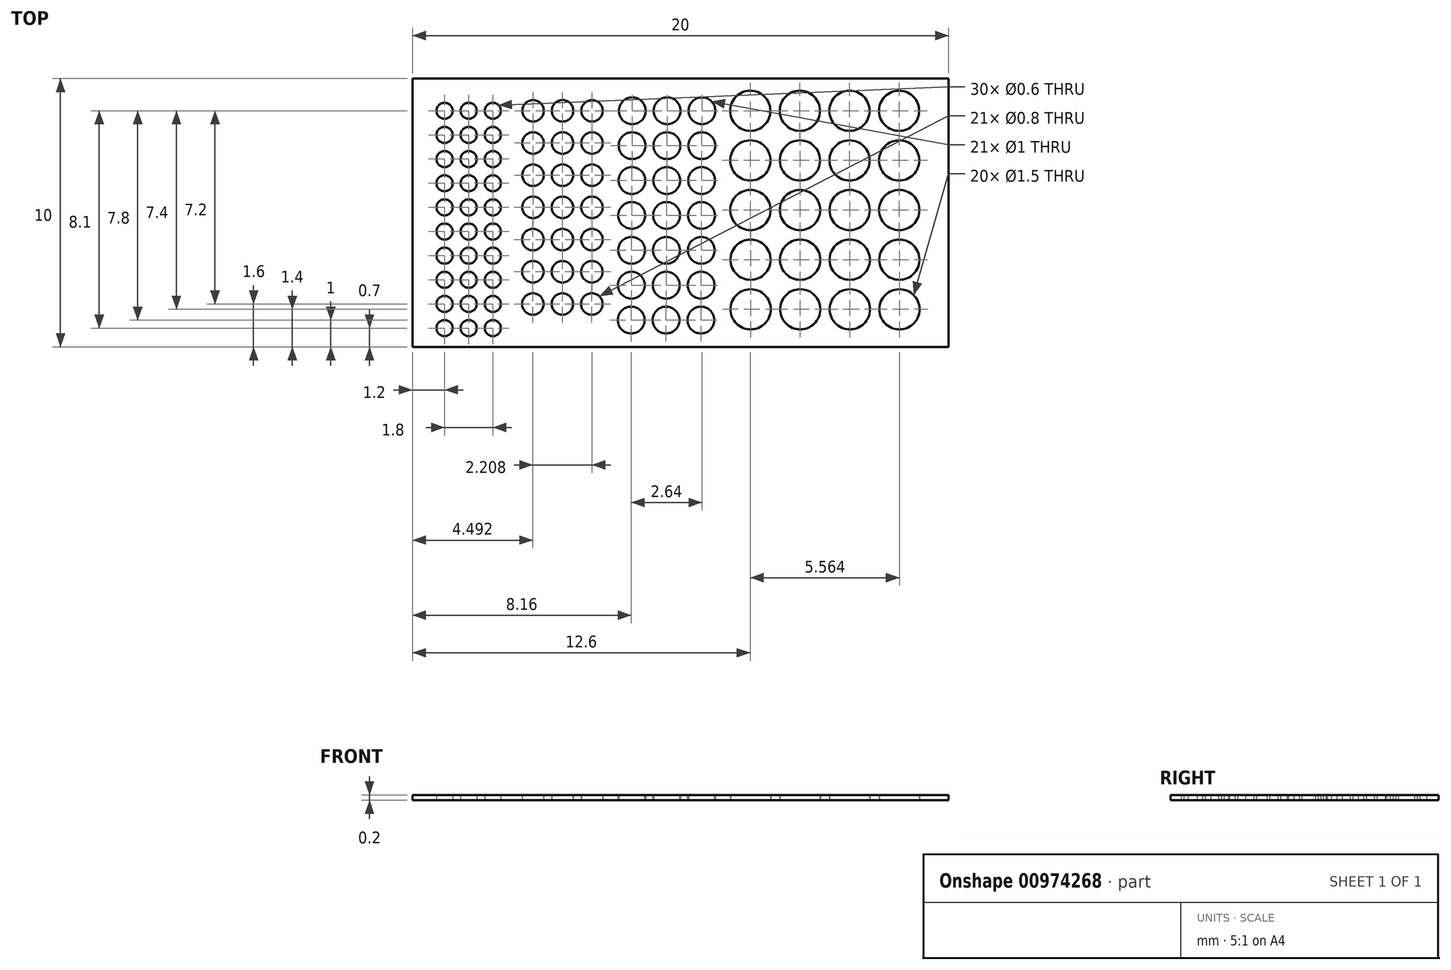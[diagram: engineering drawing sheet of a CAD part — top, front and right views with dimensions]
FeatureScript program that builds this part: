
annotation { "Feature Type Name" : "Feature", "Feature Type Description" : "" }
export const myFeature = defineFeature(function(context is Context, id is Id, definition is map)
    precondition{}
    {
        {
            var Q0;
            Q0=qCreatedBy(makeId("Top.planeOp"),FACE);
            var sketch = newSketch(context, id + "F0", { "sketchPlane" : qUnion([Q0])});
            skLineSegment(sketch, "E0.bottom", {"start": v(0, 0) * mm, "end": v(20, 0) * mm});
            skLineSegment(sketch, "E0.top", {"start": v(0, -10) * mm, "end": v(20, -10) * mm});
            skLineSegment(sketch, "E0.left", {"start": v(0, 0) * mm, "end": v(0, -10) * mm});
            skLineSegment(sketch, "E0.right", {"start": v(20, 0) * mm, "end": v(20, -10) * mm});
            skEllipse(sketch, "E1", {"center": v(1.2, -1.2) * mm, "majorRadius": 0.3 * mm, "minorRadius": 0.3 * mm, "majorAxis": v(0.93, 0.38)});
            skEllipse(sketch, "E2.1.0.0", {"center": v(2.1, -1.2) * mm, "majorRadius": 0.3 * mm, "minorRadius": 0.3 * mm, "majorAxis": v(0.93, 0.38)});
            skEllipse(sketch, "E2.2.0.0", {"center": v(3, -1.2) * mm, "majorRadius": 0.3 * mm, "minorRadius": 0.3 * mm, "majorAxis": v(0.93, 0.38)});
            skLineSegment(sketch, "E2.direction1", {"start": v(1.2, -1.2) * mm, "end": v(2.1, -1.2) * mm, "construction": true});
            skCircle(sketch, "E3", {"center": v(4.5, -1.2) * mm, "radius": 0.4 * mm});
            skCircle(sketch, "E4", {"center": v(8.2, -1.2) * mm, "radius": 0.5 * mm});
            skCircle(sketch, "E5", {"center": v(12.6, -1.2) * mm, "radius": 0.75 * mm});
            skCircle(sketch, "E6.1.0.0", {"center": v(5.6, -1.2) * mm, "radius": 0.4 * mm});
            skCircle(sketch, "E6.2.0.0", {"center": v(6.7, -1.2) * mm, "radius": 0.4 * mm});
            skLineSegment(sketch, "E6.direction1", {"start": v(4.5, -1.2) * mm, "end": v(5.6, -1.2) * mm, "construction": true});
            skCircle(sketch, "E7.1.0.0", {"center": v(4.5, -2.4) * mm, "radius": 0.4 * mm});
            skLineSegment(sketch, "E7.1.0.1", {"start": v(4.5, -2.4) * mm, "end": v(5.6, -2.4) * mm, "construction": true});
            skCircle(sketch, "E7.1.0.2", {"center": v(5.6, -2.4) * mm, "radius": 0.4 * mm});
            skCircle(sketch, "E7.1.0.3", {"center": v(6.7, -2.4) * mm, "radius": 0.4 * mm});
            skCircle(sketch, "E7.2.0.0", {"center": v(4.5, -3.6) * mm, "radius": 0.4 * mm});
            skLineSegment(sketch, "E7.2.0.1", {"start": v(4.5, -3.6) * mm, "end": v(5.6, -3.6) * mm, "construction": true});
            skCircle(sketch, "E7.2.0.2", {"center": v(5.6, -3.6) * mm, "radius": 0.4 * mm});
            skCircle(sketch, "E7.2.0.3", {"center": v(6.7, -3.6) * mm, "radius": 0.4 * mm});
            skCircle(sketch, "E7.3.0.0", {"center": v(4.5, -4.8) * mm, "radius": 0.4 * mm});
            skLineSegment(sketch, "E7.3.0.1", {"start": v(4.5, -4.8) * mm, "end": v(5.6, -4.8) * mm, "construction": true});
            skCircle(sketch, "E7.3.0.2", {"center": v(5.6, -4.8) * mm, "radius": 0.4 * mm});
            skCircle(sketch, "E7.3.0.3", {"center": v(6.7, -4.8) * mm, "radius": 0.4 * mm});
            skCircle(sketch, "E7.4.0.0", {"center": v(4.5, -6) * mm, "radius": 0.4 * mm});
            skLineSegment(sketch, "E7.4.0.1", {"start": v(4.5, -6) * mm, "end": v(5.6, -6) * mm, "construction": true});
            skCircle(sketch, "E7.4.0.2", {"center": v(5.6, -6) * mm, "radius": 0.4 * mm});
            skCircle(sketch, "E7.4.0.3", {"center": v(6.7, -6) * mm, "radius": 0.4 * mm});
            skCircle(sketch, "E7.5.0.0", {"center": v(4.5, -7.2) * mm, "radius": 0.4 * mm});
            skLineSegment(sketch, "E7.5.0.1", {"start": v(4.5, -7.2) * mm, "end": v(5.6, -7.2) * mm, "construction": true});
            skCircle(sketch, "E7.5.0.2", {"center": v(5.6, -7.2) * mm, "radius": 0.4 * mm});
            skCircle(sketch, "E7.5.0.3", {"center": v(6.7, -7.2) * mm, "radius": 0.4 * mm});
            skCircle(sketch, "E7.6.0.0", {"center": v(4.5, -8.4) * mm, "radius": 0.4 * mm});
            skLineSegment(sketch, "E7.6.0.1", {"start": v(4.5, -8.4) * mm, "end": v(5.6, -8.4) * mm, "construction": true});
            skCircle(sketch, "E7.6.0.2", {"center": v(5.6, -8.4) * mm, "radius": 0.4 * mm});
            skCircle(sketch, "E7.6.0.3", {"center": v(6.7, -8.4) * mm, "radius": 0.4 * mm});
            skLineSegment(sketch, "E7.direction1", {"start": v(4.5, -1.2) * mm, "end": v(4.5, -2.4) * mm, "construction": true});
            skCircle(sketch, "E8.1.0.0", {"center": v(14.45, -1.2) * mm, "radius": 0.75 * mm});
            skCircle(sketch, "E8.2.0.0", {"center": v(16.3, -1.2) * mm, "radius": 0.75 * mm});
            skCircle(sketch, "E8.3.0.0", {"center": v(18.15, -1.2) * mm, "radius": 0.75 * mm});
            skLineSegment(sketch, "E8.direction1", {"start": v(12.6, -1.2) * mm, "end": v(14.45, -1.2) * mm, "construction": true});
            skCircle(sketch, "E9.1.0.0", {"center": v(18.15, -3.05) * mm, "radius": 0.75 * mm});
            skLineSegment(sketch, "E9.1.0.1", {"start": v(12.6, -3.05) * mm, "end": v(14.45, -3.05) * mm, "construction": true});
            skCircle(sketch, "E9.1.0.2", {"center": v(14.45, -3.05) * mm, "radius": 0.75 * mm});
            skCircle(sketch, "E9.1.0.3", {"center": v(12.6, -3.05) * mm, "radius": 0.75 * mm});
            skCircle(sketch, "E9.1.0.4", {"center": v(16.3, -3.05) * mm, "radius": 0.75 * mm});
            skCircle(sketch, "E9.2.0.0", {"center": v(18.16, -4.9) * mm, "radius": 0.75 * mm});
            skLineSegment(sketch, "E9.2.0.1", {"start": v(12.6, -4.9) * mm, "end": v(14.46, -4.9) * mm, "construction": true});
            skCircle(sketch, "E9.2.0.2", {"center": v(14.46, -4.9) * mm, "radius": 0.75 * mm});
            skCircle(sketch, "E9.2.0.3", {"center": v(12.6, -4.9) * mm, "radius": 0.75 * mm});
            skCircle(sketch, "E9.2.0.4", {"center": v(16.3, -4.9) * mm, "radius": 0.75 * mm});
            skCircle(sketch, "E9.3.0.0", {"center": v(18.16, -6.75) * mm, "radius": 0.75 * mm});
            skLineSegment(sketch, "E9.3.0.1", {"start": v(12.61, -6.75) * mm, "end": v(14.46, -6.75) * mm, "construction": true});
            skCircle(sketch, "E9.3.0.2", {"center": v(14.46, -6.75) * mm, "radius": 0.75 * mm});
            skCircle(sketch, "E9.3.0.3", {"center": v(12.61, -6.75) * mm, "radius": 0.75 * mm});
            skCircle(sketch, "E9.3.0.4", {"center": v(16.31, -6.75) * mm, "radius": 0.75 * mm});
            skCircle(sketch, "E9.4.0.0", {"center": v(18.16, -8.6) * mm, "radius": 0.75 * mm});
            skLineSegment(sketch, "E9.4.0.1", {"start": v(12.61, -8.6) * mm, "end": v(14.46, -8.6) * mm, "construction": true});
            skCircle(sketch, "E9.4.0.2", {"center": v(14.46, -8.6) * mm, "radius": 0.75 * mm});
            skCircle(sketch, "E9.4.0.3", {"center": v(12.61, -8.6) * mm, "radius": 0.75 * mm});
            skCircle(sketch, "E9.4.0.4", {"center": v(16.31, -8.6) * mm, "radius": 0.75 * mm});
            skLineSegment(sketch, "E9.direction1", {"start": v(12.6, -1.2) * mm, "end": v(12.6, -3.05) * mm, "construction": true});
            skCircle(sketch, "E10.1.0.0", {"center": v(9.5, -1.2) * mm, "radius": 0.5 * mm});
            skCircle(sketch, "E10.2.0.0", {"center": v(10.8, -1.2) * mm, "radius": 0.5 * mm});
            skLineSegment(sketch, "E10.direction1", {"start": v(8.2, -1.2) * mm, "end": v(9.5, -1.2) * mm, "construction": true});
            skCircle(sketch, "E11.1.0.0", {"center": v(9.5, -2.5) * mm, "radius": 0.5 * mm});
            skCircle(sketch, "E11.1.0.1", {"center": v(10.8, -2.5) * mm, "radius": 0.5 * mm});
            skCircle(sketch, "E11.1.0.2", {"center": v(8.2, -2.5) * mm, "radius": 0.5 * mm});
            skLineSegment(sketch, "E11.1.0.3", {"start": v(8.2, -2.5) * mm, "end": v(9.5, -2.5) * mm, "construction": true});
            skCircle(sketch, "E11.2.0.0", {"center": v(9.49, -3.8) * mm, "radius": 0.5 * mm});
            skCircle(sketch, "E11.2.0.1", {"center": v(10.79, -3.8) * mm, "radius": 0.5 * mm});
            skCircle(sketch, "E11.2.0.2", {"center": v(8.19, -3.8) * mm, "radius": 0.5 * mm});
            skLineSegment(sketch, "E11.2.0.3", {"start": v(8.19, -3.8) * mm, "end": v(9.49, -3.8) * mm, "construction": true});
            skCircle(sketch, "E11.3.0.0", {"center": v(9.48, -5.1) * mm, "radius": 0.5 * mm});
            skCircle(sketch, "E11.3.0.1", {"center": v(10.78, -5.1) * mm, "radius": 0.5 * mm});
            skCircle(sketch, "E11.3.0.2", {"center": v(8.18, -5.1) * mm, "radius": 0.5 * mm});
            skLineSegment(sketch, "E11.3.0.3", {"start": v(8.18, -5.1) * mm, "end": v(9.48, -5.1) * mm, "construction": true});
            skCircle(sketch, "E11.4.0.0", {"center": v(9.47, -6.4) * mm, "radius": 0.5 * mm});
            skCircle(sketch, "E11.4.0.1", {"center": v(10.77, -6.4) * mm, "radius": 0.5 * mm});
            skCircle(sketch, "E11.4.0.2", {"center": v(8.17, -6.4) * mm, "radius": 0.5 * mm});
            skLineSegment(sketch, "E11.4.0.3", {"start": v(8.17, -6.4) * mm, "end": v(9.47, -6.4) * mm, "construction": true});
            skCircle(sketch, "E11.5.0.0", {"center": v(9.47, -7.7) * mm, "radius": 0.5 * mm});
            skCircle(sketch, "E11.5.0.1", {"center": v(10.77, -7.7) * mm, "radius": 0.5 * mm});
            skCircle(sketch, "E11.5.0.2", {"center": v(8.17, -7.7) * mm, "radius": 0.5 * mm});
            skLineSegment(sketch, "E11.5.0.3", {"start": v(8.17, -7.7) * mm, "end": v(9.47, -7.7) * mm, "construction": true});
            skCircle(sketch, "E11.6.0.0", {"center": v(9.46, -9) * mm, "radius": 0.5 * mm});
            skCircle(sketch, "E11.6.0.1", {"center": v(10.76, -9) * mm, "radius": 0.5 * mm});
            skCircle(sketch, "E11.6.0.2", {"center": v(8.16, -9) * mm, "radius": 0.5 * mm});
            skLineSegment(sketch, "E11.6.0.3", {"start": v(8.16, -9) * mm, "end": v(9.46, -9) * mm, "construction": true});
            skLineSegment(sketch, "E11.direction1", {"start": v(8.2, -1.2) * mm, "end": v(8.2, -2.5) * mm, "construction": true});
            skEllipse(sketch, "E12.MirrorC", {"center": v(2.1, -1.2) * mm, "majorRadius": 0.3 * mm, "minorRadius": 0.3 * mm, "majorAxis": v(0.93, -0.38)});
            skEllipse(sketch, "E13.MirrorC", {"center": v(1.2, -1.2) * mm, "majorRadius": 0.3 * mm, "minorRadius": 0.3 * mm, "majorAxis": v(0.93, -0.38)});
            skEllipse(sketch, "E14.MirrorC", {"center": v(3, -1.2) * mm, "majorRadius": 0.3 * mm, "minorRadius": 0.3 * mm, "majorAxis": v(0.93, -0.38)});
            skEllipse(sketch, "E15.1.0.0", {"center": v(2.1, -2.1) * mm, "majorRadius": 0.3 * mm, "minorRadius": 0.3 * mm, "majorAxis": v(0.93, 0.38)});
            skEllipse(sketch, "E15.1.0.1", {"center": v(1.2, -2.1) * mm, "majorRadius": 0.3 * mm, "minorRadius": 0.3 * mm, "majorAxis": v(0.93, -0.38)});
            skEllipse(sketch, "E15.1.0.2", {"center": v(3, -2.1) * mm, "majorRadius": 0.3 * mm, "minorRadius": 0.3 * mm, "majorAxis": v(0.93, 0.38)});
            skLineSegment(sketch, "E15.1.0.3", {"start": v(1.2, -2.1) * mm, "end": v(2.1, -2.1) * mm, "construction": true});
            skEllipse(sketch, "E15.1.0.4", {"center": v(1.2, -2.1) * mm, "majorRadius": 0.3 * mm, "minorRadius": 0.3 * mm, "majorAxis": v(0.93, 0.38)});
            skEllipse(sketch, "E15.1.0.5", {"center": v(3, -2.1) * mm, "majorRadius": 0.3 * mm, "minorRadius": 0.3 * mm, "majorAxis": v(0.93, -0.38)});
            skEllipse(sketch, "E15.1.0.6", {"center": v(2.1, -2.1) * mm, "majorRadius": 0.3 * mm, "minorRadius": 0.3 * mm, "majorAxis": v(0.93, -0.38)});
            skEllipse(sketch, "E15.2.0.0", {"center": v(2.1, -3) * mm, "majorRadius": 0.3 * mm, "minorRadius": 0.3 * mm, "majorAxis": v(0.93, 0.38)});
            skEllipse(sketch, "E15.2.0.1", {"center": v(1.2, -3) * mm, "majorRadius": 0.3 * mm, "minorRadius": 0.3 * mm, "majorAxis": v(0.93, -0.38)});
            skEllipse(sketch, "E15.2.0.2", {"center": v(3, -3) * mm, "majorRadius": 0.3 * mm, "minorRadius": 0.3 * mm, "majorAxis": v(0.93, 0.38)});
            skLineSegment(sketch, "E15.2.0.3", {"start": v(1.2, -3) * mm, "end": v(2.1, -3) * mm, "construction": true});
            skEllipse(sketch, "E15.2.0.4", {"center": v(1.2, -3) * mm, "majorRadius": 0.3 * mm, "minorRadius": 0.3 * mm, "majorAxis": v(0.93, 0.38)});
            skEllipse(sketch, "E15.2.0.5", {"center": v(3, -3) * mm, "majorRadius": 0.3 * mm, "minorRadius": 0.3 * mm, "majorAxis": v(0.93, -0.38)});
            skEllipse(sketch, "E15.2.0.6", {"center": v(2.1, -3) * mm, "majorRadius": 0.3 * mm, "minorRadius": 0.3 * mm, "majorAxis": v(0.93, -0.38)});
            skEllipse(sketch, "E15.3.0.0", {"center": v(2.1, -3.9) * mm, "majorRadius": 0.3 * mm, "minorRadius": 0.3 * mm, "majorAxis": v(0.93, 0.38)});
            skEllipse(sketch, "E15.3.0.1", {"center": v(1.2, -3.9) * mm, "majorRadius": 0.3 * mm, "minorRadius": 0.3 * mm, "majorAxis": v(0.93, -0.38)});
            skEllipse(sketch, "E15.3.0.2", {"center": v(3, -3.9) * mm, "majorRadius": 0.3 * mm, "minorRadius": 0.3 * mm, "majorAxis": v(0.93, 0.38)});
            skLineSegment(sketch, "E15.3.0.3", {"start": v(1.2, -3.9) * mm, "end": v(2.1, -3.9) * mm, "construction": true});
            skEllipse(sketch, "E15.3.0.4", {"center": v(1.2, -3.9) * mm, "majorRadius": 0.3 * mm, "minorRadius": 0.3 * mm, "majorAxis": v(0.93, 0.38)});
            skEllipse(sketch, "E15.3.0.5", {"center": v(3, -3.9) * mm, "majorRadius": 0.3 * mm, "minorRadius": 0.3 * mm, "majorAxis": v(0.93, -0.38)});
            skEllipse(sketch, "E15.3.0.6", {"center": v(2.1, -3.9) * mm, "majorRadius": 0.3 * mm, "minorRadius": 0.3 * mm, "majorAxis": v(0.93, -0.38)});
            skEllipse(sketch, "E15.4.0.0", {"center": v(2.1, -4.8) * mm, "majorRadius": 0.3 * mm, "minorRadius": 0.3 * mm, "majorAxis": v(0.93, 0.38)});
            skEllipse(sketch, "E15.4.0.1", {"center": v(1.2, -4.8) * mm, "majorRadius": 0.3 * mm, "minorRadius": 0.3 * mm, "majorAxis": v(0.93, -0.38)});
            skEllipse(sketch, "E15.4.0.2", {"center": v(3, -4.8) * mm, "majorRadius": 0.3 * mm, "minorRadius": 0.3 * mm, "majorAxis": v(0.93, 0.38)});
            skLineSegment(sketch, "E15.4.0.3", {"start": v(1.2, -4.8) * mm, "end": v(2.1, -4.8) * mm, "construction": true});
            skEllipse(sketch, "E15.4.0.4", {"center": v(1.2, -4.8) * mm, "majorRadius": 0.3 * mm, "minorRadius": 0.3 * mm, "majorAxis": v(0.93, 0.38)});
            skEllipse(sketch, "E15.4.0.5", {"center": v(3, -4.8) * mm, "majorRadius": 0.3 * mm, "minorRadius": 0.3 * mm, "majorAxis": v(0.93, -0.38)});
            skEllipse(sketch, "E15.4.0.6", {"center": v(2.1, -4.8) * mm, "majorRadius": 0.3 * mm, "minorRadius": 0.3 * mm, "majorAxis": v(0.93, -0.38)});
            skEllipse(sketch, "E15.5.0.0", {"center": v(2.1, -5.7) * mm, "majorRadius": 0.3 * mm, "minorRadius": 0.3 * mm, "majorAxis": v(0.93, 0.38)});
            skEllipse(sketch, "E15.5.0.1", {"center": v(1.2, -5.7) * mm, "majorRadius": 0.3 * mm, "minorRadius": 0.3 * mm, "majorAxis": v(0.93, -0.38)});
            skEllipse(sketch, "E15.5.0.2", {"center": v(3, -5.7) * mm, "majorRadius": 0.3 * mm, "minorRadius": 0.3 * mm, "majorAxis": v(0.93, 0.38)});
            skLineSegment(sketch, "E15.5.0.3", {"start": v(1.2, -5.7) * mm, "end": v(2.1, -5.7) * mm, "construction": true});
            skEllipse(sketch, "E15.5.0.4", {"center": v(1.2, -5.7) * mm, "majorRadius": 0.3 * mm, "minorRadius": 0.3 * mm, "majorAxis": v(0.93, 0.38)});
            skEllipse(sketch, "E15.5.0.5", {"center": v(3, -5.7) * mm, "majorRadius": 0.3 * mm, "minorRadius": 0.3 * mm, "majorAxis": v(0.93, -0.38)});
            skEllipse(sketch, "E15.5.0.6", {"center": v(2.1, -5.7) * mm, "majorRadius": 0.3 * mm, "minorRadius": 0.3 * mm, "majorAxis": v(0.93, -0.38)});
            skEllipse(sketch, "E15.6.0.0", {"center": v(2.1, -6.6) * mm, "majorRadius": 0.3 * mm, "minorRadius": 0.3 * mm, "majorAxis": v(0.93, 0.38)});
            skEllipse(sketch, "E15.6.0.1", {"center": v(1.2, -6.6) * mm, "majorRadius": 0.3 * mm, "minorRadius": 0.3 * mm, "majorAxis": v(0.93, -0.38)});
            skEllipse(sketch, "E15.6.0.2", {"center": v(3, -6.6) * mm, "majorRadius": 0.3 * mm, "minorRadius": 0.3 * mm, "majorAxis": v(0.93, 0.38)});
            skLineSegment(sketch, "E15.6.0.3", {"start": v(1.2, -6.6) * mm, "end": v(2.1, -6.6) * mm, "construction": true});
            skEllipse(sketch, "E15.6.0.4", {"center": v(1.2, -6.6) * mm, "majorRadius": 0.3 * mm, "minorRadius": 0.3 * mm, "majorAxis": v(0.93, 0.38)});
            skEllipse(sketch, "E15.6.0.5", {"center": v(3, -6.6) * mm, "majorRadius": 0.3 * mm, "minorRadius": 0.3 * mm, "majorAxis": v(0.93, -0.38)});
            skEllipse(sketch, "E15.6.0.6", {"center": v(2.1, -6.6) * mm, "majorRadius": 0.3 * mm, "minorRadius": 0.3 * mm, "majorAxis": v(0.93, -0.38)});
            skEllipse(sketch, "E15.7.0.0", {"center": v(2.1, -7.5) * mm, "majorRadius": 0.3 * mm, "minorRadius": 0.3 * mm, "majorAxis": v(0.93, 0.38)});
            skEllipse(sketch, "E15.7.0.1", {"center": v(1.2, -7.5) * mm, "majorRadius": 0.3 * mm, "minorRadius": 0.3 * mm, "majorAxis": v(0.93, -0.38)});
            skEllipse(sketch, "E15.7.0.2", {"center": v(3, -7.5) * mm, "majorRadius": 0.3 * mm, "minorRadius": 0.3 * mm, "majorAxis": v(0.93, 0.38)});
            skLineSegment(sketch, "E15.7.0.3", {"start": v(1.2, -7.5) * mm, "end": v(2.1, -7.5) * mm, "construction": true});
            skEllipse(sketch, "E15.7.0.4", {"center": v(1.2, -7.5) * mm, "majorRadius": 0.3 * mm, "minorRadius": 0.3 * mm, "majorAxis": v(0.93, 0.38)});
            skEllipse(sketch, "E15.7.0.5", {"center": v(3, -7.5) * mm, "majorRadius": 0.3 * mm, "minorRadius": 0.3 * mm, "majorAxis": v(0.93, -0.38)});
            skEllipse(sketch, "E15.7.0.6", {"center": v(2.1, -7.5) * mm, "majorRadius": 0.3 * mm, "minorRadius": 0.3 * mm, "majorAxis": v(0.93, -0.38)});
            skEllipse(sketch, "E15.8.0.0", {"center": v(2.1, -8.4) * mm, "majorRadius": 0.3 * mm, "minorRadius": 0.3 * mm, "majorAxis": v(0.93, 0.38)});
            skEllipse(sketch, "E15.8.0.1", {"center": v(1.2, -8.4) * mm, "majorRadius": 0.3 * mm, "minorRadius": 0.3 * mm, "majorAxis": v(0.93, -0.38)});
            skEllipse(sketch, "E15.8.0.2", {"center": v(3, -8.4) * mm, "majorRadius": 0.3 * mm, "minorRadius": 0.3 * mm, "majorAxis": v(0.93, 0.38)});
            skLineSegment(sketch, "E15.8.0.3", {"start": v(1.2, -8.4) * mm, "end": v(2.1, -8.4) * mm, "construction": true});
            skEllipse(sketch, "E15.8.0.4", {"center": v(1.2, -8.4) * mm, "majorRadius": 0.3 * mm, "minorRadius": 0.3 * mm, "majorAxis": v(0.93, 0.38)});
            skEllipse(sketch, "E15.8.0.5", {"center": v(3, -8.4) * mm, "majorRadius": 0.3 * mm, "minorRadius": 0.3 * mm, "majorAxis": v(0.93, -0.38)});
            skEllipse(sketch, "E15.8.0.6", {"center": v(2.1, -8.4) * mm, "majorRadius": 0.3 * mm, "minorRadius": 0.3 * mm, "majorAxis": v(0.93, -0.38)});
            skLineSegment(sketch, "E15.direction1", {"start": v(1.2, -1.2) * mm, "end": v(1.2, -2.1) * mm, "construction": true});
            skEllipse(sketch, "E16.0.9.0", {"center": v(2.1, -9.3) * mm, "majorRadius": 0.3 * mm, "minorRadius": 0.3 * mm, "majorAxis": v(0.93, 0.38)});
            skEllipse(sketch, "E16.2.9.0", {"center": v(1.2, -9.3) * mm, "majorRadius": 0.3 * mm, "minorRadius": 0.3 * mm, "majorAxis": v(0.93, -0.38)});
            skEllipse(sketch, "E16.4.9.0", {"center": v(3, -9.3) * mm, "majorRadius": 0.3 * mm, "minorRadius": 0.3 * mm, "majorAxis": v(0.93, 0.38)});
            skLineSegment(sketch, "E16.6.9.0", {"start": v(1.2, -9.3) * mm, "end": v(2.1, -9.3) * mm, "construction": true});
            skEllipse(sketch, "E16.9.9.0", {"center": v(1.2, -9.3) * mm, "majorRadius": 0.3 * mm, "minorRadius": 0.3 * mm, "majorAxis": v(0.93, 0.38)});
            skEllipse(sketch, "E16.11.9.0", {"center": v(3, -9.3) * mm, "majorRadius": 0.3 * mm, "minorRadius": 0.3 * mm, "majorAxis": v(0.93, -0.38)});
            skEllipse(sketch, "E16.13.9.0", {"center": v(2.1, -9.3) * mm, "majorRadius": 0.3 * mm, "minorRadius": 0.3 * mm, "majorAxis": v(0.93, -0.38)});
            skSolve(sketch);
        }
        {
            var Q0;
            Q0=makeQuery(id+"F0.imprint","IMPRINT",FACE,{"disambiguationData":[TD([[makeQuery(id+"F0.imprint","IMPRINT",EDGE,{"derivedFrom":sQuery(id+"F0.wireOp",EDGE,"E0.bottom")}),-1.0]])]});
            extrude(context, id + "F1", {"entities" : qUnion([Q0]), "depth" : 0.2 * mm, "offsetDistance" : 25.4 * mm});
        }
    });
